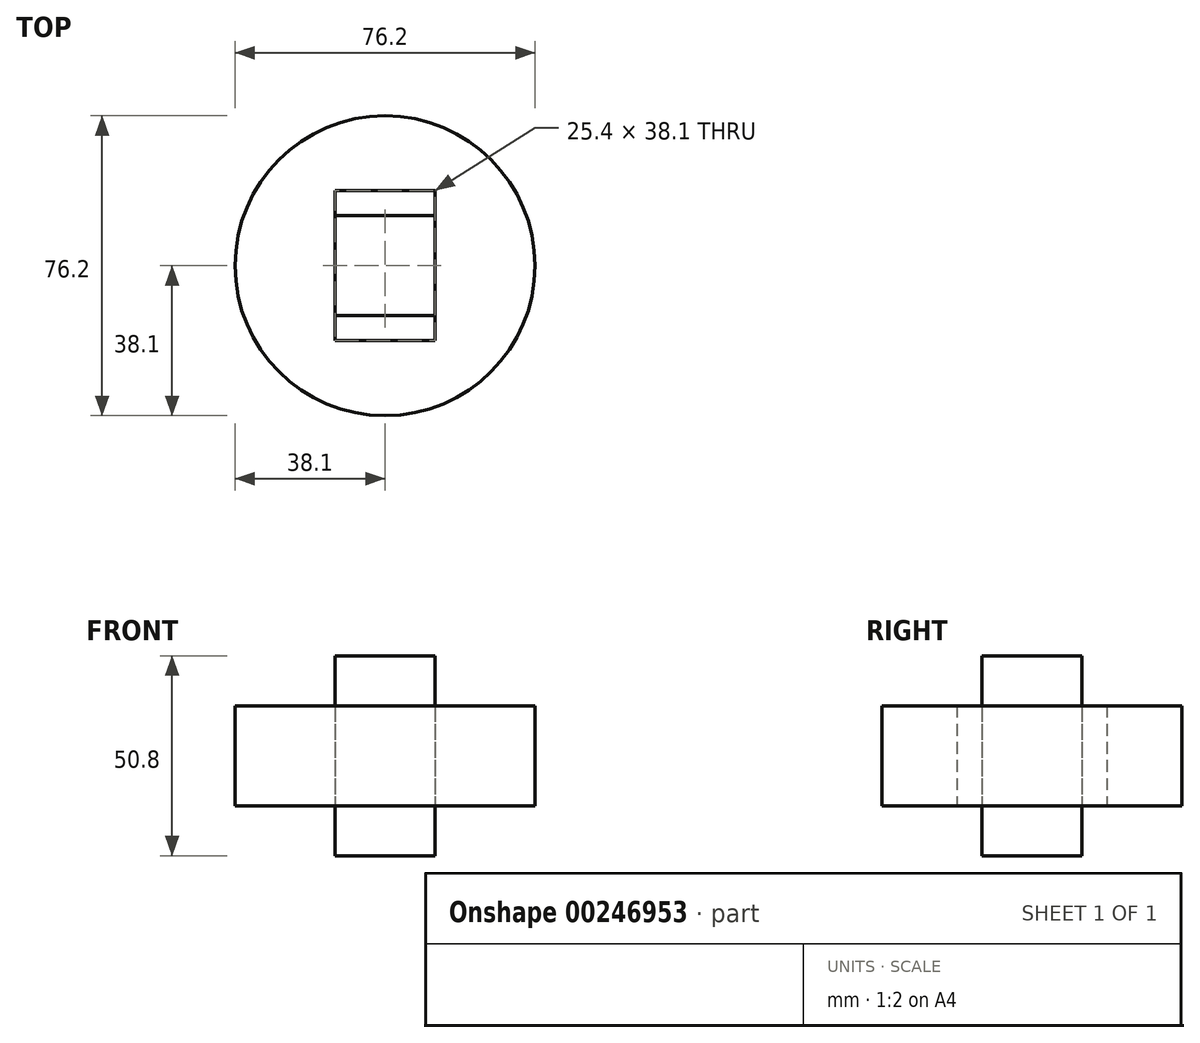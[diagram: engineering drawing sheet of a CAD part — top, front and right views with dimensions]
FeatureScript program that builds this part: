
annotation { "Feature Type Name" : "Feature", "Feature Type Description" : "" }
export const myFeature = defineFeature(function(context is Context, id is Id, definition is map)
    precondition{}
    {
        {
            var Q0;
            Q0=qCreatedBy(makeId("Top.planeOp"),FACE);
            var sketch = newSketch(context, id + "F0", { "sketchPlane" : qUnion([Q0])});
            skCircle(sketch, "E0", {"center": v(0, 0) * mm, "radius": 38.1 * mm});
            skSolve(sketch);
        }
        {
            var Q0;
            Q0 = qSketchRegion(id + "F0", true);
            extrude(context, id + "F1", {"entities" : qUnion([Q0]), "endBound" : BoundingType.SYMMETRIC, "depth" : 25.4 * mm});
        }
        {
            var Q0;
            Q0=qCreatedBy(makeId("Top.planeOp"),FACE);
            var sketch = newSketch(context, id + "F2", { "sketchPlane" : qUnion([Q0])});
            skLineSegment(sketch, "E1.bottom", {"start": v(12.7, -12.7) * mm, "end": v(-12.7, -12.7) * mm});
            skLineSegment(sketch, "E1.top", {"start": v(12.7, 12.7) * mm, "end": v(-12.7, 12.7) * mm});
            skLineSegment(sketch, "E1.left", {"start": v(12.7, -12.7) * mm, "end": v(12.7, 12.7) * mm});
            skLineSegment(sketch, "E1.right", {"start": v(-12.7, -12.7) * mm, "end": v(-12.7, 12.7) * mm});
            skPoint(sketch, "E1.middle", {"position": v(0, 0) * mm});
            skSolve(sketch);
        }
        {
            var Q0;
            Q0=makeQuery(id+"F2.imprint","IMPRINT",FACE,{"disambiguationData":[TD([[makeQuery(id+"F2.imprint","IMPRINT",EDGE,{"derivedFrom":sQuery(id+"F2.wireOp",EDGE,"E1.bottom")}),-1.0]])]});
            extrude(context, id + "F3", {"entities" : qUnion([Q0]), "endBound" : BoundingType.SYMMETRIC, "depth" : 50.8 * mm});
        }
        {
            var Q0;
            Q0=makeQuery(id+"F3.opExtrude","SWEPT_BODY",BODY,{"disambiguationData":[OSD([sQuery(id+"F2.wireOp",EDGE,"E1.bottom"),sQuery(id+"F2.wireOp",EDGE,"E1.top"),sQuery(id+"F2.wireOp",EDGE,"E1.left"),sQuery(id+"F2.wireOp",EDGE,"E1.right")])]});
            var Q1;
            Q1=makeQuery(id+"F1.opExtrude","SWEPT_BODY",BODY,{"disambiguationData":[OSD([sQuery(id+"F0.wireOp",EDGE,"E0")])]});
            var Q2;
            Q2=makeQuery(id+"F3.opExtrude","SWEPT_FACE",FACE,{"disambiguationData":[OSD([sQuery(id+"F2.wireOp",EDGE,"E1.top")])]});
            var Q3;
            Q3=makeQuery(id+"F3.opExtrude","SWEPT_FACE",FACE,{"disambiguationData":[OSD([sQuery(id+"F2.wireOp",EDGE,"E1.bottom")])]});
            booleanBodies(context, id + "F4", {"operationType" : BooleanOperationType.SUBTRACTION, "tools" : qUnion([Q0]), "targets" : qUnion([Q1]), "offset" : true, "entitiesToOffset" : qUnion([Q2, Q3]), "offsetDistance" : 6.35 * mm, "keepTools" : true});
        }
    });
